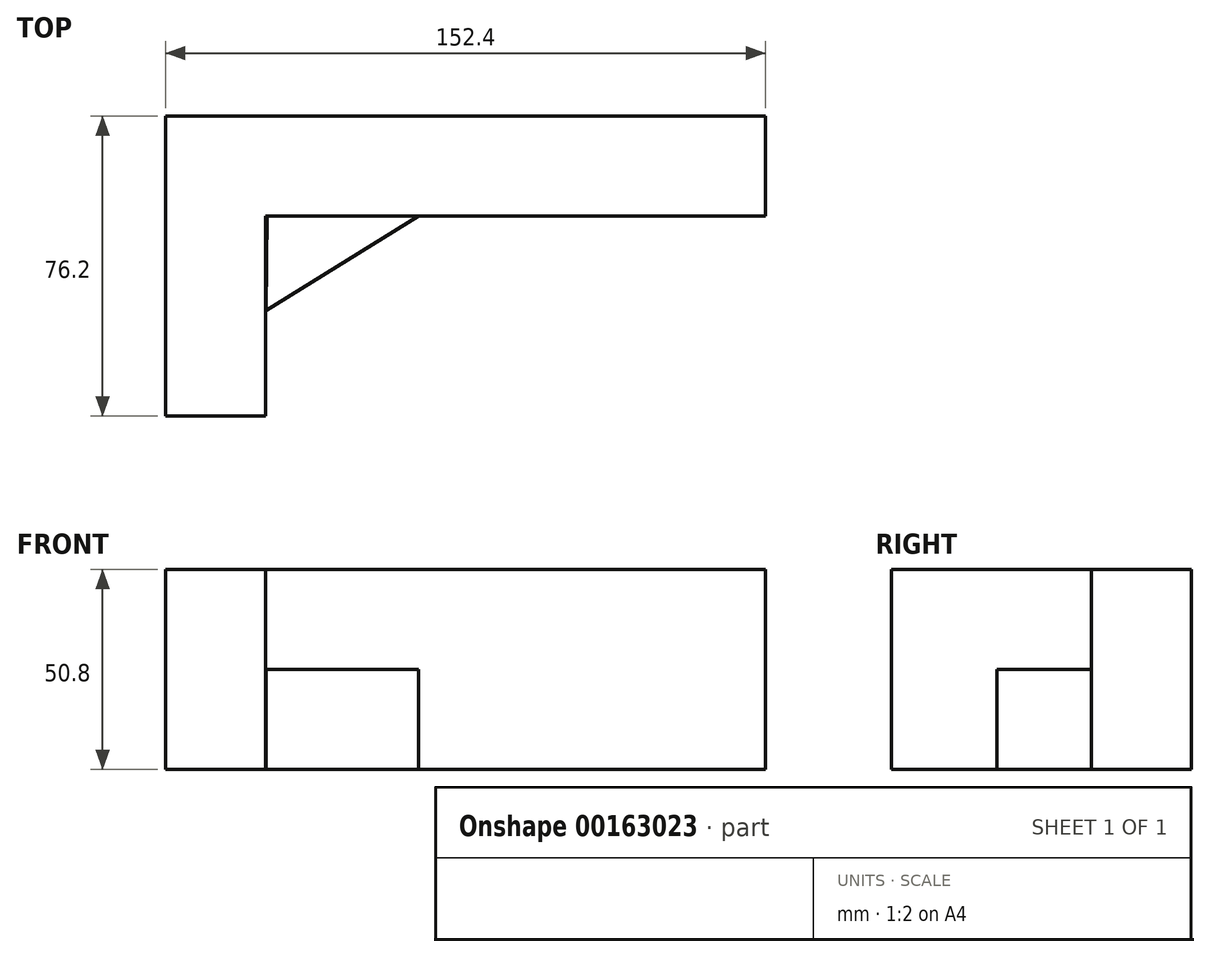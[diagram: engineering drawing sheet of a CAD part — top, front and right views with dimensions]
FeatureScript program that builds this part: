
annotation { "Feature Type Name" : "Feature", "Feature Type Description" : "" }
export const myFeature = defineFeature(function(context is Context, id is Id, definition is map)
    precondition{}
    {
        {
            var Q0;
            Q0=qCreatedBy(makeId("Top.planeOp"),FACE);
            var sketch = newSketch(context, id + "F0", { "sketchPlane" : qUnion([Q0])});
            skLineSegment(sketch, "E0", {"start": v(0, 0) * mm, "end": v(0, 76.2) * mm});
            skLineSegment(sketch, "E1", {"start": v(0, 76.2) * mm, "end": v(152.4, 76.2) * mm});
            skLineSegment(sketch, "E2", {"start": v(152.4, 76.2) * mm, "end": v(152.4, 50.8) * mm});
            skLineSegment(sketch, "E3", {"start": v(152.4, 50.8) * mm, "end": v(25.4, 50.8) * mm});
            skLineSegment(sketch, "E4", {"start": v(25.4, 50.8) * mm, "end": v(25.4, 0) * mm});
            skLineSegment(sketch, "E5", {"start": v(25.4, 0) * mm, "end": v(0, 0) * mm});
            skSolve(sketch);
        }
        {
            var Q0;
            Q0=makeQuery(id+"F0.imprint","IMPRINT",FACE,{"disambiguationData":[TD([[makeQuery(id+"F0.imprint","IMPRINT",EDGE,{"derivedFrom":sQuery(id+"F0.wireOp",EDGE,"E0")}),-1.0]])]});
            extrude(context, id + "F1", {"entities" : qUnion([Q0]), "depth" : 50.8 * mm});
        }
        {
            var Q0;
            Q0=qCreatedBy(makeId("Top.planeOp"),FACE);
            var sketch = newSketch(context, id + "F2", { "sketchPlane" : qUnion([Q0])});
            skLineSegment(sketch, "E6", {"start": v(25.55, 26.85) * mm, "end": v(64.68, 51.03) * mm});
            skLineSegment(sketch, "E7", {"start": v(64.68, 51.03) * mm, "end": v(25.73, 51.03) * mm});
            skLineSegment(sketch, "E8", {"start": v(25.73, 51.03) * mm, "end": v(25.55, 26.85) * mm});
            skSolve(sketch);
        }
        {
            var Q0;
            Q0 = qSketchRegion(id + "F2", true);
            extrude(context, id + "F3", {"entities" : qUnion([Q0]), "operationType" : NewBodyOperationType.ADD, "depth" : 25.4 * mm});
        }
    });
